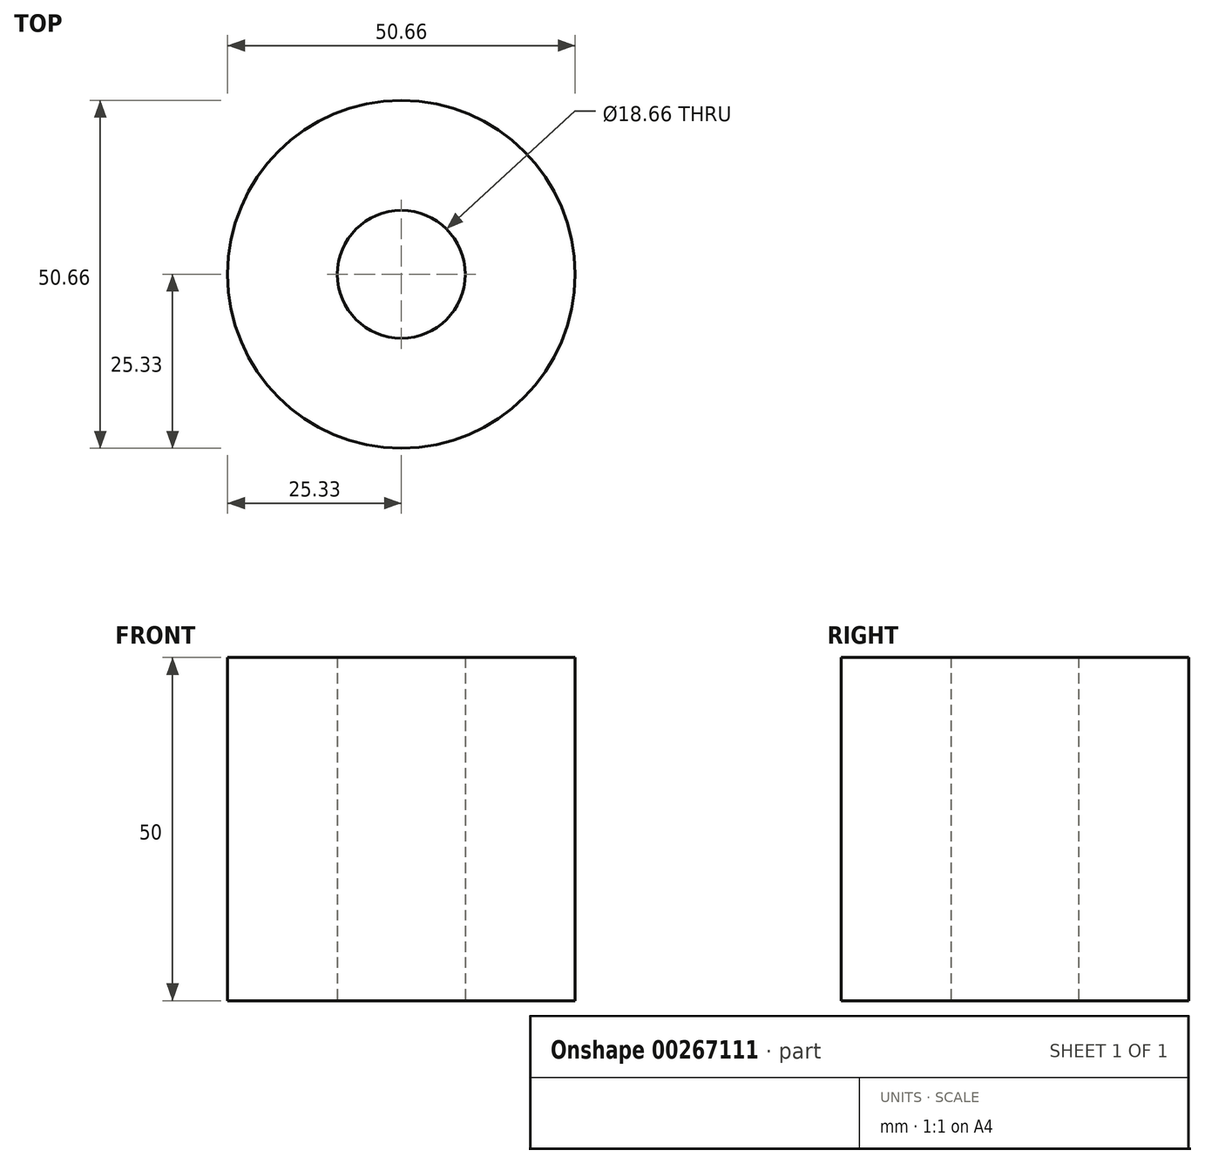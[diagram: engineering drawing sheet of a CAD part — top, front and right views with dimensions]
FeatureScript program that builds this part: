
annotation { "Feature Type Name" : "Feature", "Feature Type Description" : "" }
export const myFeature = defineFeature(function(context is Context, id is Id, definition is map)
    precondition{}
    {
        {
            var Q0;
            Q0=qCreatedBy(makeId("Top.planeOp"),FACE);
            var sketch = newSketch(context, id + "F0", { "sketchPlane" : qUnion([Q0])});
            skCircle(sketch, "E0", {"center": v(0, 0) * mm, "radius": 25.33 * mm});
            skCircle(sketch, "E1", {"center": v(0, 0) * mm, "radius": 9.33 * mm});
            skSolve(sketch);
        }
        {
            var Q0;
            Q0 = qSketchRegion(id + "F0", true);
            extrude(context, id + "F1", {"entities" : qUnion([Q0]), "depth" : 50 * mm});
        }
        {
            var Q0;
            Q0=makeQuery(id+"F1.opExtrude","CAP_FACE",FACE,{"disambiguationData":[OSD([sQuery(id+"F0.wireOp",EDGE,"E0"),sQuery(id+"F0.wireOp",EDGE,"E1")])],"isStart":false});
            cPlane(context, id + "F2", {"entities" : qUnion([Q0]), "cplaneType" : CPlaneType.OFFSET, "offset" : 8 * mm, "oppositeDirection" : true, "width" : 150 * mm, "height" : 150 * mm});
        }
        {
            var Q0;
            Q0=qCreatedBy(id+"F2.planeOp",FACE);
            var sketch = newSketch(context, id + "F3", { "sketchPlane" : qUnion([Q0])});
            skLineSegment(sketch, "E2", {"start": v(0, 0) * mm, "end": v(17.91, 17.91) * mm, "construction": true});
            skLineSegment(sketch, "E3", {"start": v(0, 0) * mm, "end": v(0, 25.33) * mm, "construction": true});
            skCircle(sketch, "E4.0", {"center": v(0, 0) * mm, "radius": 25.33 * mm, "construction": true});
            skSolve(sketch);
        }
    });
